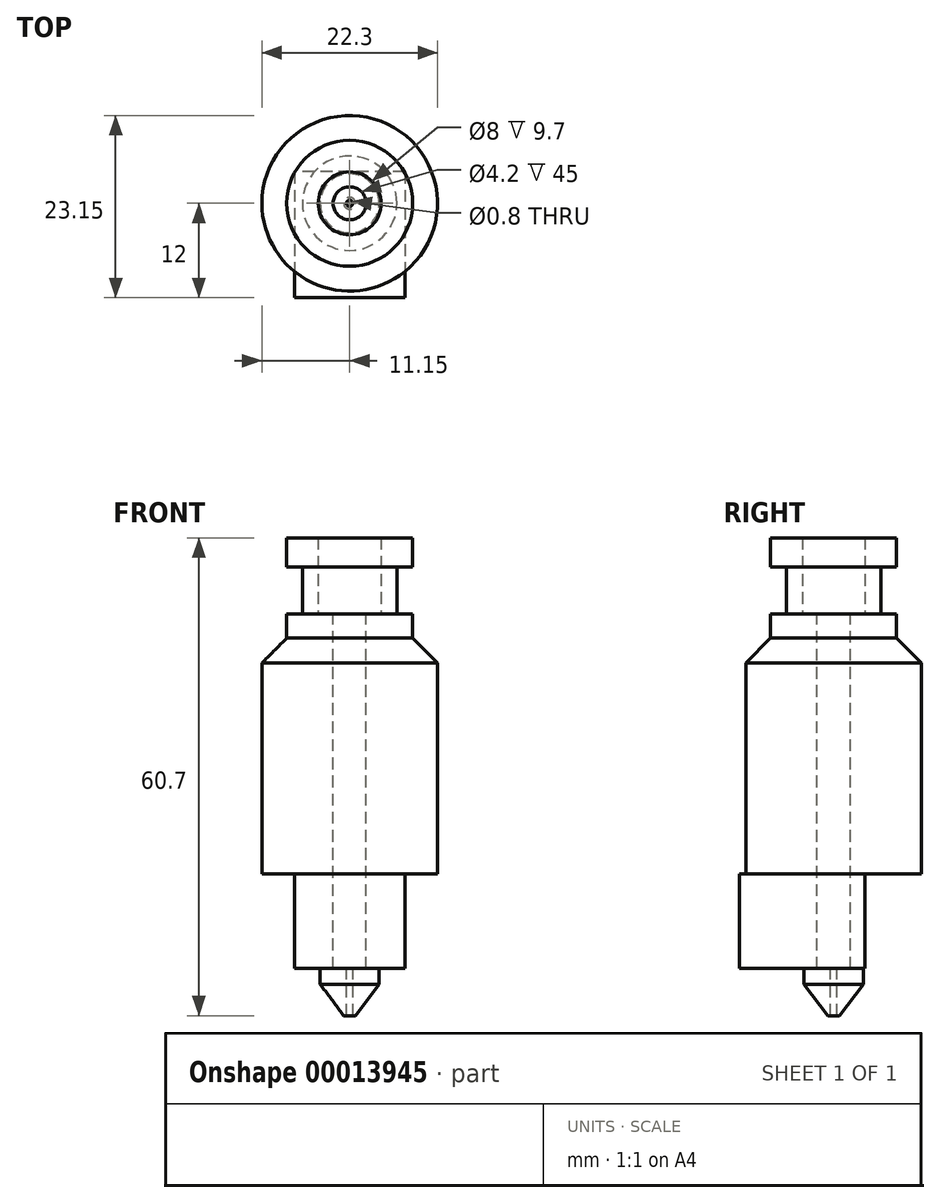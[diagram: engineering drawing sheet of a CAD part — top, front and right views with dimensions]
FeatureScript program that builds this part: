
annotation { "Feature Type Name" : "Feature", "Feature Type Description" : "" }
export const myFeature = defineFeature(function(context is Context, id is Id, definition is map)
    precondition{}
    {
        {
            var Q0;
            Q0=qCreatedBy(makeId("Top.planeOp"),FACE);
            var sketch = newSketch(context, id + "F0", { "sketchPlane" : qUnion([Q0])});
            skCircle(sketch, "E0", {"center": v(0, 0) * mm, "radius": 8 * mm});
            skCircle(sketch, "E1", {"center": v(0, 0) * mm, "radius": 4 * mm});
            skSolve(sketch);
        }
        {
            var Q0;
            Q0 = qSketchRegion(id + "F0", true);
            extrude(context, id + "F1", {"entities" : qUnion([Q0]), "depth" : 3.7 * mm});
        }
        {
            var Q0;
            Q0=makeQuery(id+"F1.opExtrude","CAP_FACE",FACE,{"disambiguationData":[OSD([sQuery(id+"F0.wireOp",EDGE,"E0"),sQuery(id+"F0.wireOp",EDGE,"E1")])],"isStart":true});
            var sketch = newSketch(context, id + "F2", { "sketchPlane" : qUnion([Q0])});
            skCircle(sketch, "E2", {"center": v(0, 0) * mm, "radius": 6 * mm});
            skSolve(sketch);
        }
        {
            var Q0;
            Q0=makeQuery(id+"F2.imprint","IMPRINT",FACE,{"disambiguationData":[TD([[makeQuery(id+"F2.imprint","IMPRINT",EDGE,{"derivedFrom":sQuery(id+"F2.wireOp",EDGE,"E2")}),1.0]])]});
            extrude(context, id + "F3", {"entities" : qUnion([Q0]), "operationType" : NewBodyOperationType.ADD, "depth" : 6 * mm});
        }
        {
            var Q0;
            Q0=makeQuery(id+"F3.opExtrude","CAP_FACE",FACE,{"disambiguationData":[OSD([sQuery(id+"F0.wireOp",EDGE,"E1"),sQuery(id+"F2.wireOp",EDGE,"E2")])],"isStart":false});
            var sketch = newSketch(context, id + "F4", { "sketchPlane" : qUnion([Q0])});
            skCircle(sketch, "E3", {"center": v(0, 0) * mm, "radius": 2.1 * mm});
            skCircle(sketch, "E4.0", {"center": v(0, 0) * mm, "radius": 8 * mm});
            skSolve(sketch);
        }
        {
            var Q0;
            Q0 = qSketchRegion(id + "F4", true);
            extrude(context, id + "F5", {"entities" : qUnion([Q0]), "operationType" : NewBodyOperationType.ADD, "depth" : 3 * mm});
        }
        {
            var Q0;
            Q0=makeQuery(id+"F5.opExtrude","CAP_FACE",FACE,{"disambiguationData":[OSD([sQuery(id+"F4.wireOp",EDGE,"E3"),sQuery(id+"F4.wireOp",EDGE,"E4.0")])],"isStart":false});
            var sketch = newSketch(context, id + "F6", { "sketchPlane" : qUnion([Q0])});
            skCircle(sketch, "E5", {"center": v(0, 0) * mm, "radius": 11.15 * mm});
            skSolve(sketch);
        }
        {
            var Q0;
            Q0=makeQuery(id+"F6.imprint","IMPRINT",FACE,{"disambiguationData":[TD([[makeQuery(id+"F6.imprint","IMPRINT",EDGE,{"derivedFrom":sQuery(id+"F6.wireOp",EDGE,"E5")}),1.0]])]});
            var Q1;
            Q1=makeQuery(id+"F6.imprint","IMPRINT",FACE,{"disambiguationData":[TD([[makeQuery(id+"F6.imprint","IMPRINT",EDGE,{"derivedFrom":makeQuery(id+"F5.opExtrude","CAP_EDGE",EDGE,{"disambiguationData":[OSD([sQuery(id+"F4.wireOp",EDGE,"E3")])],"isStart":false})}),-1.0]])]});
            extrude(context, id + "F7", {"entities" : qUnion([Q0, Q1]), "operationType" : NewBodyOperationType.ADD, "depth" : 30 * mm});
        }
        {
            var Q0;
            Q0=makeQuery(id+"F7.opExtrude","CAP_EDGE",EDGE,{"disambiguationData":[OSD([sQuery(id+"F6.wireOp",EDGE,"E5")])],"isStart":true});
            chamfer(context, id + "F8", {"entities" : qUnion([Q0]), "width" : 3.2 * mm});
        }
        {
            var Q0;
            Q0=makeQuery(id+"F7.opExtrude","CAP_FACE",FACE,{"disambiguationData":[OSD([sQuery(id+"F4.wireOp",EDGE,"E3"),sQuery(id+"F6.wireOp",EDGE,"E5")])],"isStart":false});
            var sketch = newSketch(context, id + "F9", { "sketchPlane" : qUnion([Q0])});
            skLineSegment(sketch, "E6.bottom", {"start": v(7, -4) * mm, "end": v(-7, -4) * mm});
            skLineSegment(sketch, "E6.top", {"start": v(7, 12) * mm, "end": v(-7, 12) * mm});
            skLineSegment(sketch, "E6.left", {"start": v(7, -4) * mm, "end": v(7, 12) * mm});
            skLineSegment(sketch, "E6.right", {"start": v(-7, -4) * mm, "end": v(-7, 12) * mm});
            skSolve(sketch);
        }
        {
            var Q0;
            {var subQ3=sQuery(id+"F9.wireOp",EDGE,"E6.top");Q0=makeQuery(id+"F9.imprint","IMPRINT",FACE,{"disambiguationData":[TD([[makeQuery(id+"F9.imprint","IMPRINT",EDGE,{"derivedFrom":subQ3}),1.0]])]});}
            var Q1;
            {var subQ5=sQuery(id+"F9.wireOp",EDGE,"E6.bottom");Q1=makeQuery(id+"F9.imprint","IMPRINT",FACE,{"disambiguationData":[TD([[makeQuery(id+"F9.imprint","IMPRINT",EDGE,{"derivedFrom":subQ5}),-1.0]])]});}
            extrude(context, id + "F10", {"entities" : qUnion([Q0, Q1]), "operationType" : NewBodyOperationType.ADD, "depth" : 12 * mm});
        }
        {
            var Q0;
            Q0=makeQuery(id+"F10.opExtrude","CAP_FACE",FACE,{"disambiguationData":[OSD([sQuery(id+"F4.wireOp",EDGE,"E3"),sQuery(id+"F9.wireOp",EDGE,"E6.bottom"),sQuery(id+"F9.wireOp",EDGE,"E6.top"),sQuery(id+"F9.wireOp",EDGE,"E6.left"),sQuery(id+"F9.wireOp",EDGE,"E6.right")])],"isStart":false});
            var sketch = newSketch(context, id + "F11", { "sketchPlane" : qUnion([Q0])});
            skCircle(sketch, "E7", {"center": v(0, 0) * mm, "radius": 3.75 * mm});
            skCircle(sketch, "E8", {"center": v(0, 0) * mm, "radius": 0.4 * mm});
            skSolve(sketch);
        }
        {
            var Q0;
            Q0 = qSketchRegion(id + "F11", true);
            extrude(context, id + "F12", {"entities" : qUnion([Q0]), "operationType" : NewBodyOperationType.ADD, "depth" : 6 * mm});
        }
        {
            var Q0;
            Q0=makeQuery(id+"F12.opExtrude","CAP_EDGE",EDGE,{"disambiguationData":[OSD([sQuery(id+"F11.wireOp",EDGE,"E7")])],"isStart":false});
            chamfer(context, id + "F13", {"entities" : qUnion([Q0]), "chamferType" : ChamferType.TWO_OFFSETS, "width1" : 3 * mm, "oppositeDirection" : false, "width2" : 4 * mm, "tangentPropagation" : true});
        }
    });
